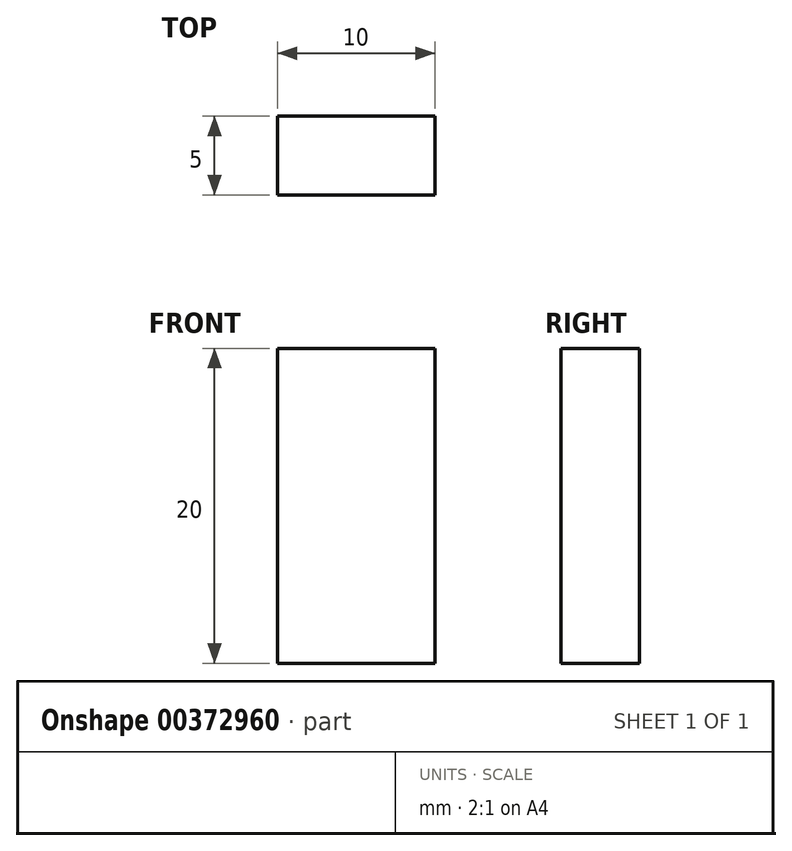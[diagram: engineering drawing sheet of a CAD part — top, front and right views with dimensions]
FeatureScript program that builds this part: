
annotation { "Feature Type Name" : "Feature", "Feature Type Description" : "" }
export const myFeature = defineFeature(function(context is Context, id is Id, definition is map)
    precondition{}
    {
        {
            var Q0;
            Q0=qCreatedBy(makeId("Top.planeOp"),FACE);
            var sketch = newSketch(context, id + "F0", { "sketchPlane" : qUnion([Q0])});
            skLineSegment(sketch, "E0.bottom", {"start": v(0, 0) * mm, "end": v(10, 0) * mm});
            skLineSegment(sketch, "E0.top", {"start": v(0, 5) * mm, "end": v(10, 5) * mm});
            skLineSegment(sketch, "E0.left", {"start": v(0, 0) * mm, "end": v(0, 5) * mm});
            skLineSegment(sketch, "E0.right", {"start": v(10, 0) * mm, "end": v(10, 5) * mm});
            skSolve(sketch);
        }
        {
            var Q0;
            Q0 = qSketchRegion(id + "F0", true);
            extrude(context, id + "F1", {"entities" : qUnion([Q0]), "depth" : 20 * mm});
        }
    });
